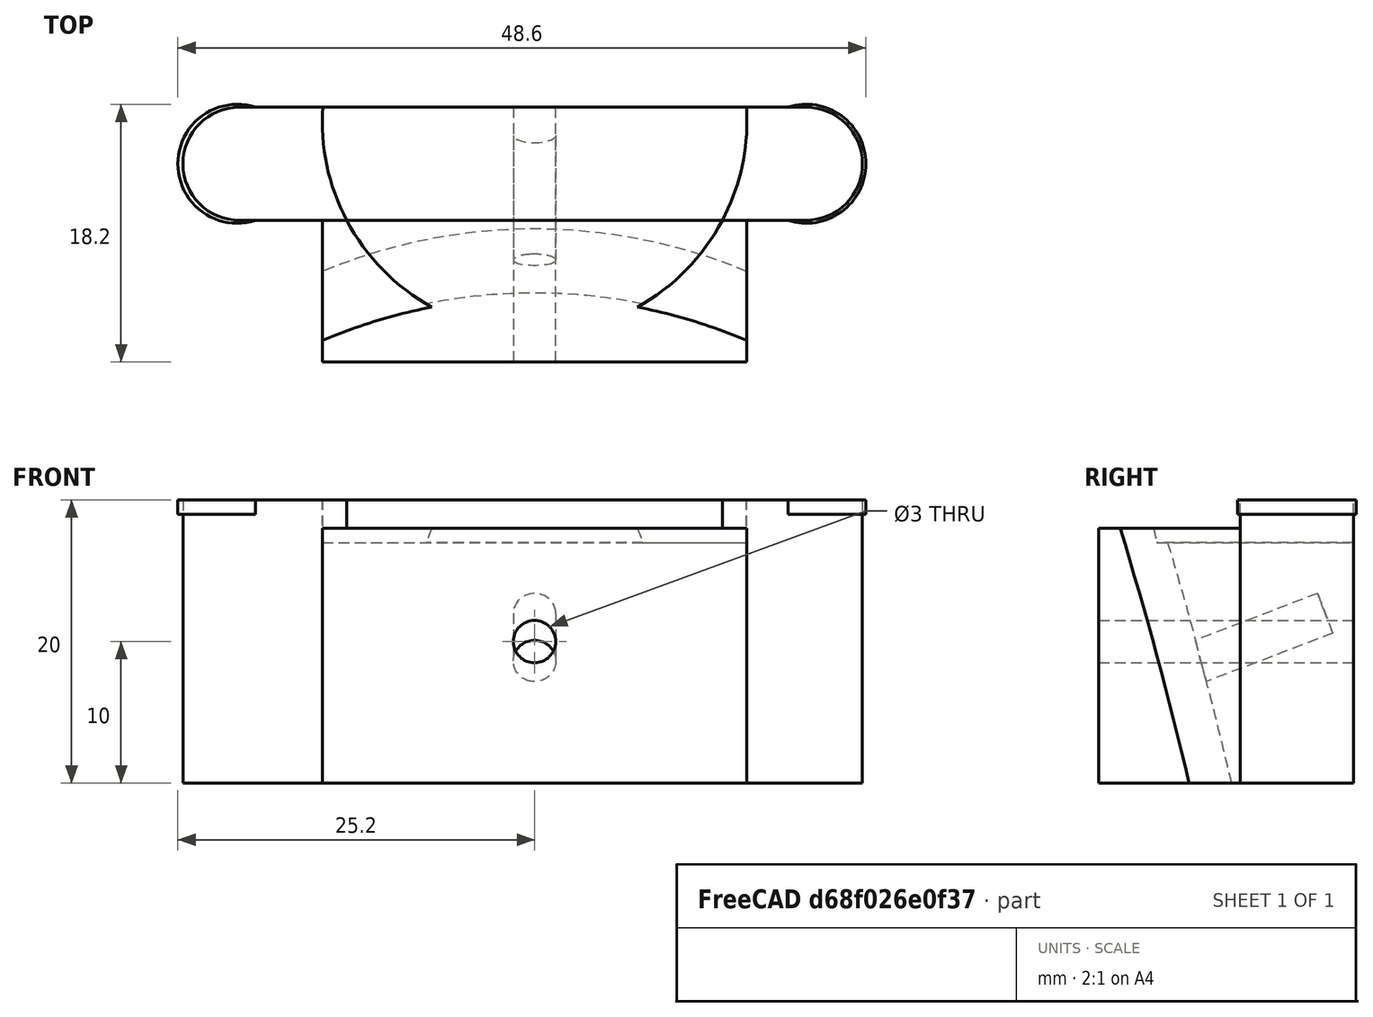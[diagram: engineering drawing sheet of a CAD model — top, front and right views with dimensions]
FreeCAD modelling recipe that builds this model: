
FCSTD DOCUMENT  (FreeCAD 0.19R)
Label: RoundTailLight
License: All rights reserved
LicenseURL: http://en.wikipedia.org/wiki/All_rights_reserved
objects: Part::Cylinder×4, Sketcher::SketchObject×3, Part::Cut×3, PartDesign::Pad×2, Part::MultiFuse×2, Part::Torus×1, PartDesign::Pocket×1, PartDesign::Body×1, Mesh::Feature×1
note: 20 computed .brp shape members not serialized (recipe doc carries the construction recipe); baked Part::Feature solids carry a one-line shape summary decoded from their .brp

FEATURE [Sketcher::SketchObject] Sketch
  FullyConstrained = false
  MapMode = 5
  Support = -> [XY_Plane]
  sketch-geometry (4):
    g0: ArcOfCircle CenterX=-20.8387 CenterY=4 CenterZ=0 NormalX=0 NormalY=0 NormalZ=1 AngleXU=0 Radius=4 StartAngle=1.5708 EndAngle=4.71239
    g1: ArcOfCircle CenterX=19.1613 CenterY=4 CenterZ=0 NormalX=0 NormalY=0 NormalZ=1 AngleXU=0 Radius=4 StartAngle=4.71239 EndAngle=7.85398
    g2: LineSegment StartX=-20.8387 StartY=0 StartZ=0 EndX=19.1613 EndY=0 EndZ=0
    g3: LineSegment StartX=-20.8387 StartY=8 StartZ=0 EndX=19.1613 EndY=8 EndZ=0
  constraints (9):
    c: Tangent(g0,g3) = 1.5708
    c: Tangent(g0,g2) = -1.5708
    c: Tangent(g2,g1) = -1.5708
    c: Tangent(g3,g1) = 1.5708
    c: Horizontal(g2)
    c: Equal(g0,g1)
    c: Tangent(g1,g-1)
    c: Radius(g1) = 4
    c: Distance(g1,g0) = 40
FEATURE [PartDesign::Pad] Pad
  Direction = (1,1,1)
  Length = 20
  Length2 = 100
  Profile = -> Sketch
  Type = 0
FEATURE [Sketcher::SketchObject] Sketch001
  FullyConstrained = true
  MapMode = 5
  Placement = pos=(0,0,0) rot=(1,0,0;1.5708rad)
  Support = -> [Pad]
  sketch-geometry (4):
    g0: LineSegment StartX=-15 StartY=18 StartZ=0 EndX=15 EndY=18 EndZ=0
    g1: LineSegment StartX=15 StartY=18 StartZ=0 EndX=15 EndY=0 EndZ=0
    g2: LineSegment StartX=15 StartY=0 StartZ=0 EndX=-15 EndY=0 EndZ=0
    g3: LineSegment StartX=-15 StartY=0 StartZ=0 EndX=-15 EndY=18 EndZ=0
  constraints (11):
    c: Coincident(g0,g1)
    c: Coincident(g1,g2)
    c: Coincident(g2,g3)
    c: Coincident(g3,g0)
    c: Horizontal(g0)
    c: Horizontal(g2)
    c: Vertical(g1)
    c: Vertical(g3)
    c: Symmetric(g1,g2,g-1)
    c: Distance(g1) = 18
    c: Distance(g0) = 30
FEATURE [PartDesign::Pad] Pad001
  BaseFeature = -> Pad
  Direction = (1,1,1)
  Length = 10
  Length2 = 100
  Profile = -> Sketch001
  Type = 0
FEATURE [Part::Torus] Torus
  Angle1 = -180
  Angle2 = 180
  Angle3 = 360
  AttacherType = Attacher::AttachEngine3D
  Placement = pos=(0,-283,-66) rot=(0,1,0;1.5708rad)
  Radius1 = 250
  Radius2 = 40
FEATURE [Sketcher::SketchObject] Sketch002
  FullyConstrained = true
  MapMode = 5
  Placement = pos=(0,8,0) rot=(0,0.707107,0.707107;3.14159rad)
  sketch-geometry (1):
    g0: Circle CenterX=0 CenterY=10 CenterZ=0 NormalX=0 NormalY=0 NormalZ=1 AngleXU=0 Radius=1.5
  constraints (3):
    c: Radius(g0) = 1.5
    c: PointOnObject(g0,g-2)
    c: DistanceY(g0) = 10
FEATURE [PartDesign::Pocket] Pocket
  BaseFeature = -> Pad001
  Length = 5
  Length2 = 100
  Profile = -> Sketch002
  Type = 1
FEATURE [PartDesign::Body] Body
  Group = -> [Sketch,Pad,Sketch001,Pad001,Sketch002,Pocket]
  Origin = -> Origin
  Tip = -> Pocket
FEATURE [Part::Cut] Cut
  Base = -> Pad001
  Tool = -> Torus
FEATURE [Part::Cylinder] Cylinder
  Angle = 360
  AttacherType = Attacher::AttachEngine3D
  Height = 10
  Placement = pos=(0,6,12) rot=(1,0,0;1.93731rad)
  Radius = 1.5
FEATURE [Part::Cut] Cut001
  Base = -> Cut
  Tool = -> Cylinder
FEATURE [Part::Cylinder] Cylinder001
  Angle = 360
  AttacherType = Attacher::AttachEngine3D
  Height = 10
  Placement = pos=(0,7,17) rot=(0,0,1;0rad)
  Radius = 15
FEATURE [Part::Cut] Cut002
  Base = -> Cut001
  Tool = -> Cylinder001
FEATURE [Part::Cylinder] Cylinder002
  Angle = 360
  AttacherType = Attacher::AttachEngine3D
  Height = 1
  Placement = pos=(-21,4,19) rot=(0,0,1;0rad)
  Radius = 4.2
FEATURE [Part::Cylinder] Cylinder003
  Angle = 360
  AttacherType = Attacher::AttachEngine3D
  Height = 1
  Placement = pos=(19.2,4,19) rot=(0,0,1;0rad)
  Radius = 4.2
FEATURE [Part::MultiFuse] Fusion
  Shapes = -> [Cut002,Cylinder002]
FEATURE [Part::MultiFuse] Fusion001
  Shapes = -> [Fusion,Cylinder003]
FEATURE [Mesh::Feature] Mesh  label="Fusion001 (Meshed)"
